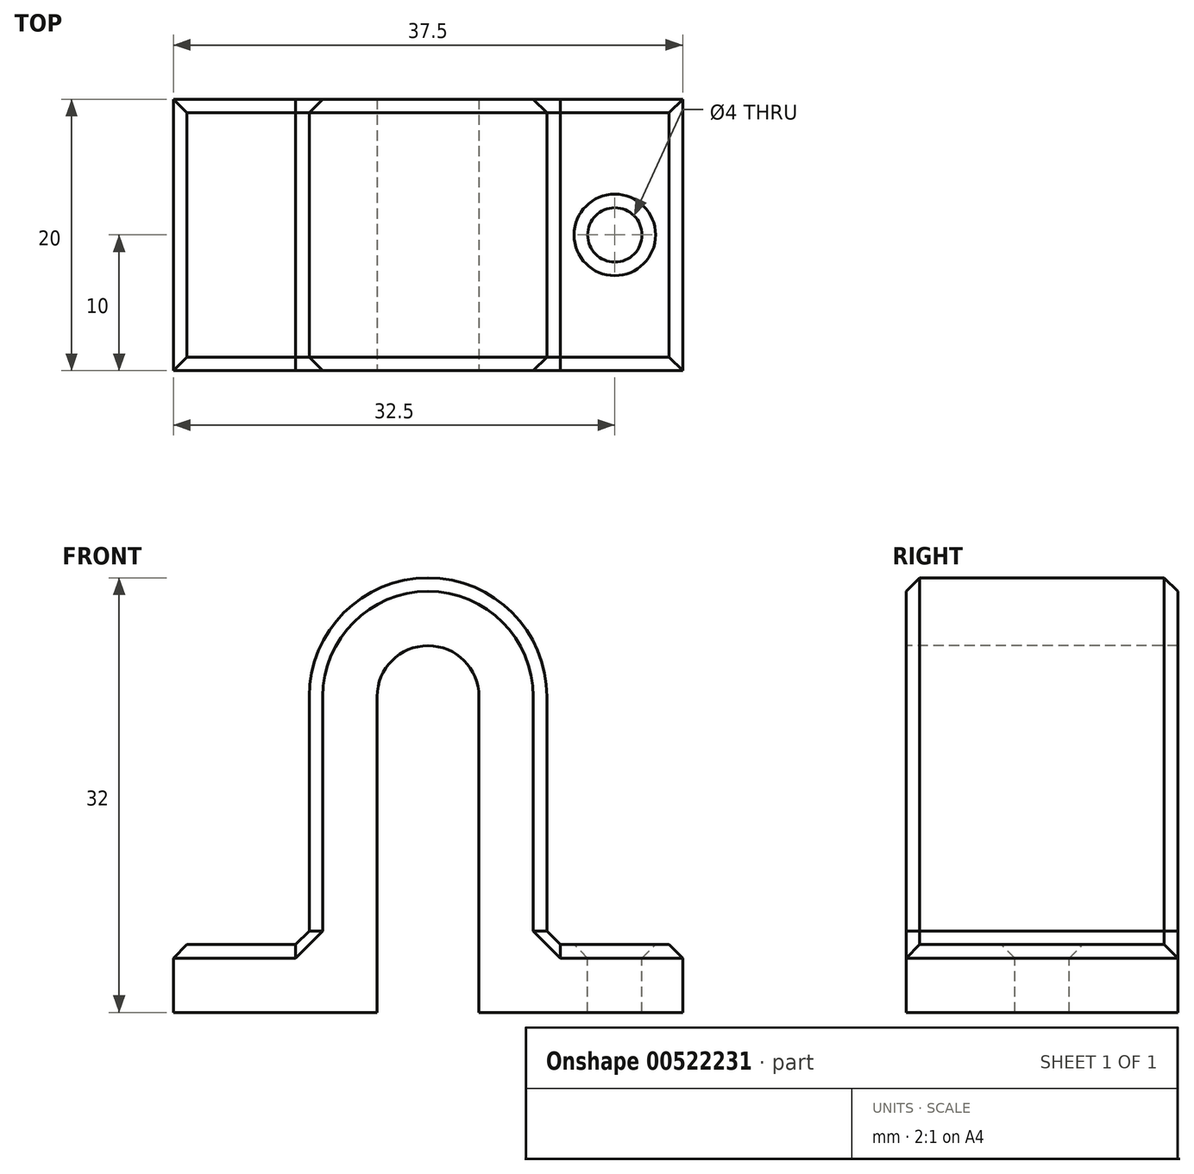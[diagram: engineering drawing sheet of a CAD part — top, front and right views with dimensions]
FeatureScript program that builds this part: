
annotation { "Feature Type Name" : "Feature", "Feature Type Description" : "" }
export const myFeature = defineFeature(function(context is Context, id is Id, definition is map)
    precondition{}
    {
        {
            var Q0;
            Q0=qCreatedBy(makeId("Front.planeOp"),FACE);
            var sketch = newSketch(context, id + "F0", { "sketchPlane" : qUnion([Q0])});
            skLineSegment(sketch, "E0", {"start": v(3.75, 0) * mm, "end": v(3.75, 23.25) * mm});
            skLineSegment(sketch, "E1.MirrorCS", {"start": v(-3.75, 0) * mm, "end": v(-3.75, 23.25) * mm});
            skArc(sketch, "E2", {"start": v(-3.75, 23.25) * mm, "mid": v(0, 27) * mm, "end": v(3.75, 23.25) * mm});
            skLineSegment(sketch, "E3", {"start": v(-3.75, 0) * mm, "end": v(-18.75, 0) * mm});
            skLineSegment(sketch, "E4", {"start": v(-18.75, 0) * mm, "end": v(-18.75, 5) * mm});
            skLineSegment(sketch, "E5", {"start": v(-18.75, 5) * mm, "end": v(-8.75, 5) * mm});
            skLineSegment(sketch, "E6", {"start": v(-8.75, 5) * mm, "end": v(-8.75, 23.25) * mm});
            skLineSegment(sketch, "E7.MirrorCS", {"start": v(8.75, 5) * mm, "end": v(8.75, 23.25) * mm});
            skLineSegment(sketch, "E8.MirrorCS", {"start": v(18.75, 5) * mm, "end": v(8.75, 5) * mm});
            skLineSegment(sketch, "E9.MirrorCS", {"start": v(18.75, 0) * mm, "end": v(18.75, 5) * mm});
            skLineSegment(sketch, "E10.MirrorCS", {"start": v(3.75, 0) * mm, "end": v(18.75, 0) * mm});
            skArc(sketch, "E11", {"start": v(-8.75, 23.25) * mm, "mid": v(0, 32) * mm, "end": v(8.75, 23.25) * mm});
            skSolve(sketch);
        }
        {
            var Q0;
            Q0=makeQuery(id+"F0.imprint","IMPRINT",FACE,{"disambiguationData":[TD([[makeQuery(id+"F0.imprint","IMPRINT",EDGE,{"derivedFrom":sQuery(id+"F0.wireOp",EDGE,"E0")}),-1.0]])]});
            extrude(context, id + "F1", {"entities" : qUnion([Q0]), "oppositeDirection" : true, "depth" : 10 * mm, "offsetDistance" : 25 * mm, "hasSecondDirection" : true, "secondDirectionOppositeDirection" : false, "secondDirectionDepth" : 10 * mm});
        }
        {
            var Q0;
            Q0=makeQuery(id+"F1.opExtrude","SWEPT_FACE",FACE,{"disambiguationData":[OSD([sQuery(id+"F0.wireOp",EDGE,"E8.MirrorCS")])]});
            var sketch = newSketch(context, id + "F2", { "sketchPlane" : qUnion([Q0])});
            skLineSegment(sketch, "E12.0.0", {"start": v(8.75, -10) * mm, "end": v(18.75, -10) * mm});
            skLineSegment(sketch, "E12.0.1", {"start": v(18.75, -10) * mm, "end": v(18.75, 10) * mm});
            skLineSegment(sketch, "E12.0.2", {"start": v(18.75, 10) * mm, "end": v(8.75, 10) * mm});
            skLineSegment(sketch, "E12.0.3", {"start": v(8.75, 10) * mm, "end": v(8.75, -10) * mm});
            skCircle(sketch, "E13", {"center": v(13.75, 0) * mm, "radius": 2 * mm});
            skPoint(sketch, "E13.centerSnap0", {"position": v(13.75, 10) * mm});
            skCircle(sketch, "E14.MirrorC", {"center": v(-13.75, 0) * mm, "radius": 2 * mm});
            skSolve(sketch);
        }
        {
            var Q0;
            Q0=makeQuery(id+"F2.imprint","IMPRINT",FACE,{"disambiguationData":[TD([[makeQuery(id+"F2.imprint","IMPRINT",EDGE,{"derivedFrom":sQuery(id+"F2.wireOp",EDGE,"E14.MirrorC")}),-1.0]])]});
            var Q1;
            Q1=makeQuery(id+"F2.imprint","IMPRINT",FACE,{"disambiguationData":[TD([[makeQuery(id+"F2.imprint","IMPRINT",EDGE,{"derivedFrom":sQuery(id+"F2.wireOp",EDGE,"E13")}),1.0]])]});
            extrude(context, id + "F3", {"entities" : qUnion([Q0, Q1]), "operationType" : NewBodyOperationType.REMOVE, "oppositeDirection" : true, "depth" : 25 * mm, "offsetDistance" : 25 * mm});
        }
        {
            var Q0;
            Q0=makeQuery(id+"F3.boolean.opBoolean","COPY",EDGE,{"derivedFrom":makeQuery(id+"F3.opExtrude","CAP_EDGE",EDGE,{"disambiguationData":[OSD([sQuery(id+"F2.wireOp",EDGE,"E13")])],"isStart":true})});
            var Q1;
            Q1=makeQuery(id+"F3.boolean.opBoolean","COPY",EDGE,{"derivedFrom":makeQuery(id+"F3.opExtrude","CAP_EDGE",EDGE,{"disambiguationData":[OSD([sQuery(id+"F2.wireOp",EDGE,"E14.MirrorC")])],"isStart":true})});
            var Q2;
            Q2=makeQuery(id+"F1.opExtrude","CAP_EDGE",EDGE,{"disambiguationData":[OSD([sQuery(id+"F0.wireOp",EDGE,"E8.MirrorCS")])],"isStart":true});
            var Q3;
            Q3=makeQuery(id+"F1.opExtrude","SWEPT_EDGE",EDGE,{"disambiguationData":[OSD([sQuery(id+"F0.wireOp",EDGE,"E8.MirrorCS"),sQuery(id+"F0.wireOp",EDGE,"E9.MirrorCS")])]});
            var Q4;
            Q4=makeQuery(id+"F1.opExtrude","SWEPT_FACE",FACE,{"disambiguationData":[OSD([sQuery(id+"F0.wireOp",EDGE,"E8.MirrorCS")])]});
            var Q5;
            Q5=makeQuery(id+"F1.opExtrude","SWEPT_FACE",FACE,{"disambiguationData":[OSD([sQuery(id+"F0.wireOp",EDGE,"E5")])]});
            chamfer(context, id + "F4", {"entities" : qUnion([Q0, Q1, Q2, Q3, Q4, Q5]), "width" : 1 * mm, "tangentPropagation" : true});
        }
    });
